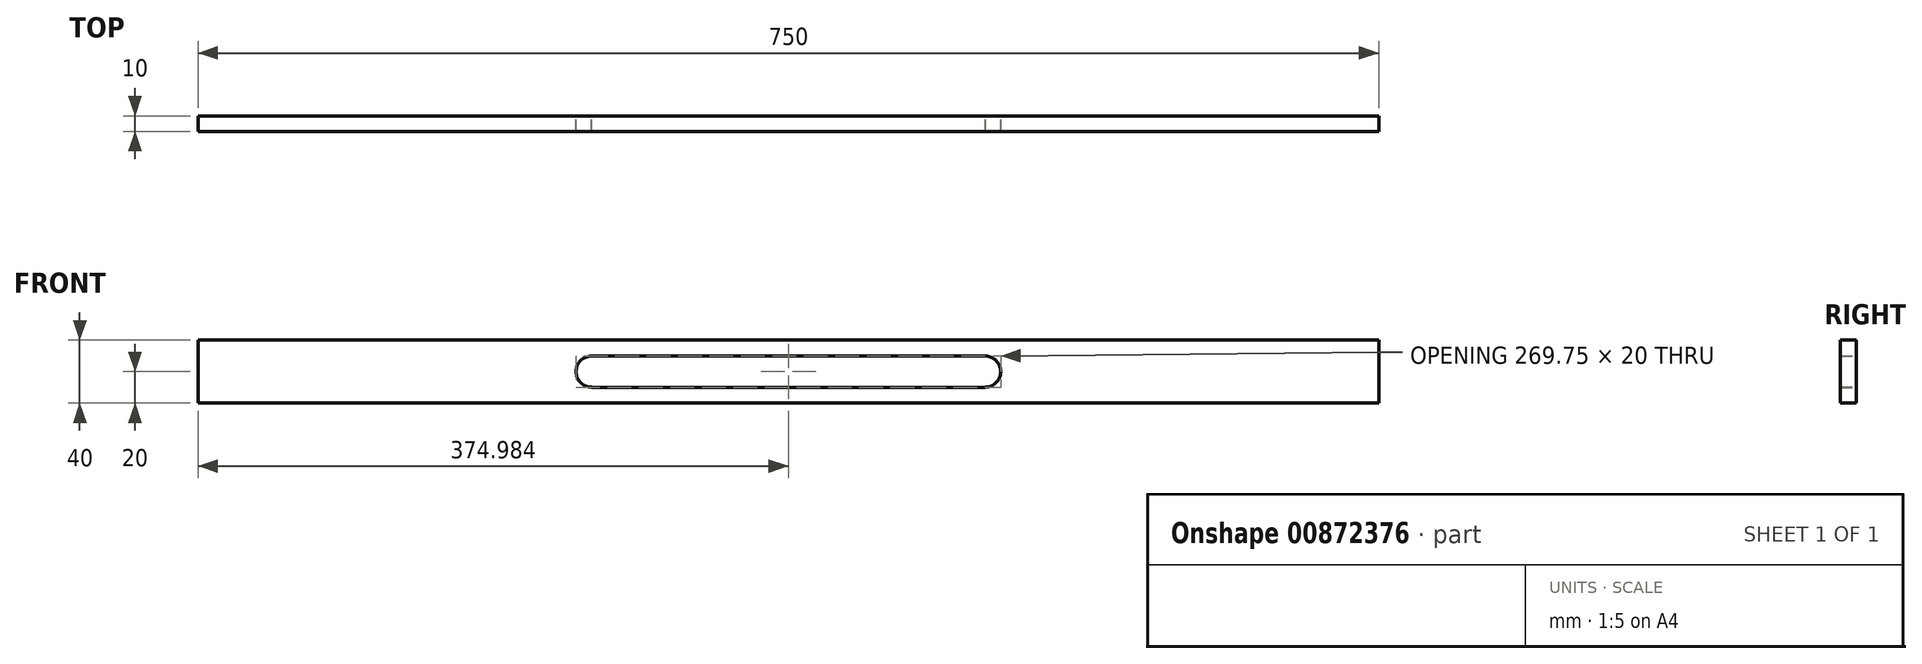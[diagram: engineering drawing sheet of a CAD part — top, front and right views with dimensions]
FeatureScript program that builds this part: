
annotation { "Feature Type Name" : "Feature", "Feature Type Description" : "" }
export const myFeature = defineFeature(function(context is Context, id is Id, definition is map)
    precondition{}
    {
        {
            var Q0;
            Q0=qCreatedBy(makeId("Front.planeOp"),FACE);
            var sketch = newSketch(context, id + "F0", { "sketchPlane" : qUnion([Q0])});
            skLineSegment(sketch, "E0.bottom", {"start": v(375, -20) * mm, "end": v(-375, -20) * mm});
            skLineSegment(sketch, "E0.top", {"start": v(375, 20) * mm, "end": v(-375, 20) * mm});
            skLineSegment(sketch, "E0.left", {"start": v(375, -20) * mm, "end": v(375, 20) * mm});
            skLineSegment(sketch, "E0.right", {"start": v(-375, -20) * mm, "end": v(-375, 20) * mm});
            skPoint(sketch, "E0.middle", {"position": v(0, 0) * mm});
            skLineSegment(sketch, "E1", {"start": v(-375, 10) * mm, "end": v(375, 10) * mm});
            skLineSegment(sketch, "E2", {"start": v(375, 10) * mm, "end": v(375, -10) * mm});
            skLineSegment(sketch, "E3", {"start": v(375, -10) * mm, "end": v(-375, -10) * mm});
            skLineSegment(sketch, "E4", {"start": v(-125, 10) * mm, "end": v(-125, -10) * mm});
            skLineSegment(sketch, "E5", {"start": v(125, 10) * mm, "end": v(125, -10) * mm});
            skCircle(sketch, "E6", {"center": v(-125, 0) * mm, "radius": 9.9 * mm});
            skCircle(sketch, "E7", {"center": v(125, 0) * mm, "radius": 9.86 * mm});
            skSolve(sketch);
        }
        {
            var Q0;
            Q0 = qSketchRegion(id + "F0", true);
            extrude(context, id + "F1", {"entities" : qUnion([Q0]), "depth" : 10 * mm, "offsetDistance" : 25 * mm});
        }
    });
